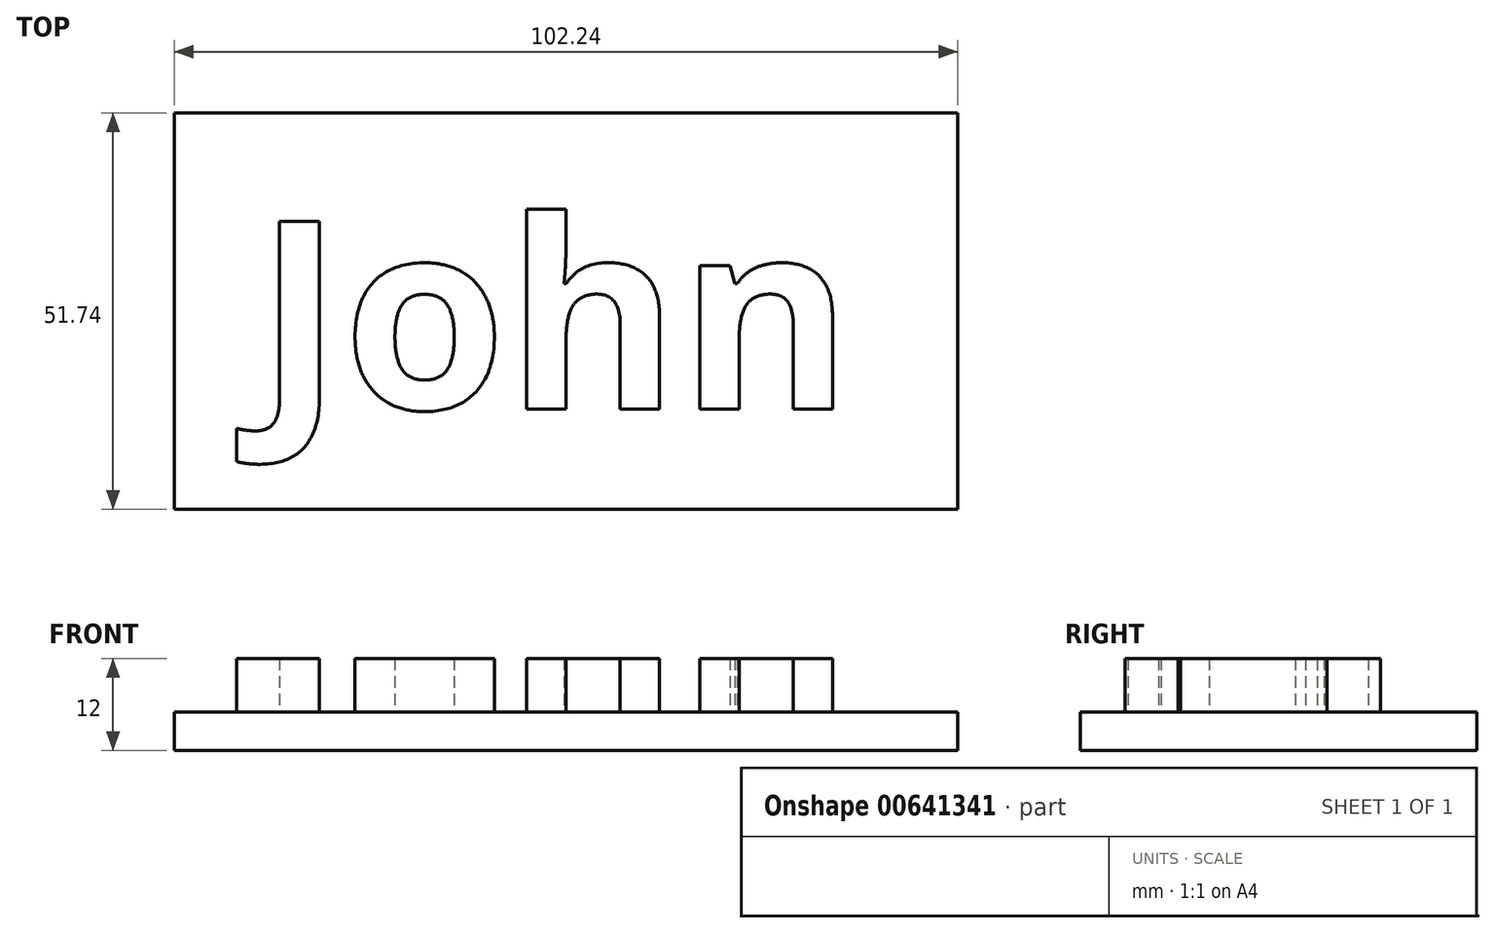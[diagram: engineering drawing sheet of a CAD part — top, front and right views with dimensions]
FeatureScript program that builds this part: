
annotation { "Feature Type Name" : "Feature", "Feature Type Description" : "" }
export const myFeature = defineFeature(function(context is Context, id is Id, definition is map)
    precondition{}
    {
        {
            var Q0;
            Q0=qCreatedBy(makeId("Top.planeOp"),FACE);
            var sketch = newSketch(context, id + "F0", { "sketchPlane" : qUnion([Q0])});
            skLineSegment(sketch, "E0.bottom", {"start": v(-47.74, 40.98) * mm, "end": v(54.5, 40.98) * mm});
            skLineSegment(sketch, "E0.top", {"start": v(-47.74, -10.76) * mm, "end": v(54.5, -10.76) * mm});
            skLineSegment(sketch, "E0.left", {"start": v(-47.74, 40.98) * mm, "end": v(-47.74, -10.76) * mm});
            skLineSegment(sketch, "E0.right", {"start": v(54.5, 40.98) * mm, "end": v(54.5, -10.76) * mm});
            skSolve(sketch);
        }
        {
            var Q0;
            Q0 = qSketchRegion(id + "F0", true);
            extrude(context, id + "F1", {"entities" : qUnion([Q0]), "depth" : 5 * mm, "offsetDistance" : 25 * mm});
        }
        {
            var Q0;
            Q0=makeQuery(id+"F1.opExtrude","CAP_FACE",FACE,{"disambiguationData":[OSD([sQuery(id+"F0.wireOp",EDGE,"E0.bottom"),sQuery(id+"F0.wireOp",EDGE,"E0.top"),sQuery(id+"F0.wireOp",EDGE,"E0.left"),sQuery(id+"F0.wireOp",EDGE,"E0.right")])],"isStart":false});
            var sketch = newSketch(context, id + "F2", { "sketchPlane" : qUnion([Q0])});
            skText(sketch, "E1", { "text": "John", "fontName": "OpenSans-Bold.ttf"});
            const initialGuessF2  = {"E1": [-0.03707, 0.00232, 1, 0, 0.02474]};
            skSetInitialGuess(sketch, initialGuessF2);
            skSolve(sketch);
        }
        {
            var Q0;
            Q0 = qSketchRegion(id + "F2", true);
            extrude(context, id + "F3", {"entities" : qUnion([Q0]), "operationType" : NewBodyOperationType.ADD, "depth" : 7 * mm, "offsetDistance" : 25 * mm});
        }
    });
